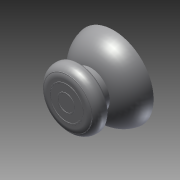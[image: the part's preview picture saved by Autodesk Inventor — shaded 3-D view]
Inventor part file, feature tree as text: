
AUTODESK INVENTOR PART (.ipt)
format: ipt  version: 2012 SP1 (Build 160190100, 190)  size: 203,776 bytes
history: native  units: in
note: dims shown in document units (in); Inventor stores cm internally (conversion verified against a paired STEP export)
features: extrude x6, fillet x6, sketch x6
ambient origin geometry x8: Origin, YZ Plane, XZ Plane, XY Plane, X Axis, Y Axis, Z Axis, Center Point
bodies: Solid1 (feature_tree)
feature tree (18):
  extrude  "Extrusion1"  Depth=0.25in TaperAngle=0.0deg
  fillet  "Fillet1"  Radius=0.3in
  extrude  "Extrusion2"  Depth=0.36in TaperAngle=0.0deg
  extrude  "Extrusion3"  Depth=0.14in TaperAngle=0.0deg
  fillet  "Fillet2"  Radius=0.1in
  fillet  "Fillet3"  Radius=0.025in
  extrude  "Extrusion4"  Depth=0.47in
  fillet  "Fillet4"  Radius=0.13in
  extrude  "Extrusion5"  Depth=0.36in
  fillet  "Fillet5"  Radius=0.33in
  extrude  "Extrusion6"  Depth=0.0025in
  fillet  "Fillet6"  Radius=0.19in
  sketch  "Sketch1"  dims[d0=0.85in d1=0.25in d2=0.0in d3=0.3in]
  sketch  "Sketch2"  dims[d4=0.4in d5=0.36in d6=0.0in]
  sketch  "Sketch3"  dims[d7=0.62in d8=0.14in d9=0.0in d10=0.1in d11=0.025in]
  sketch  "Sketch4"  dims[d12=0.52in d13=0.47in d14=0.13in d15=0.0in]
  sketch  "Sketch5"  dims[d16=0.0025in d17=0.36in d18=0.33in]
  sketch  "Sketch6"  dims[d19=0.1425in d20=0.0in d21=0.0025in d22=0.19in d23=0.16in d24=0.0025in d25=0.0in d26=0.0025in]
